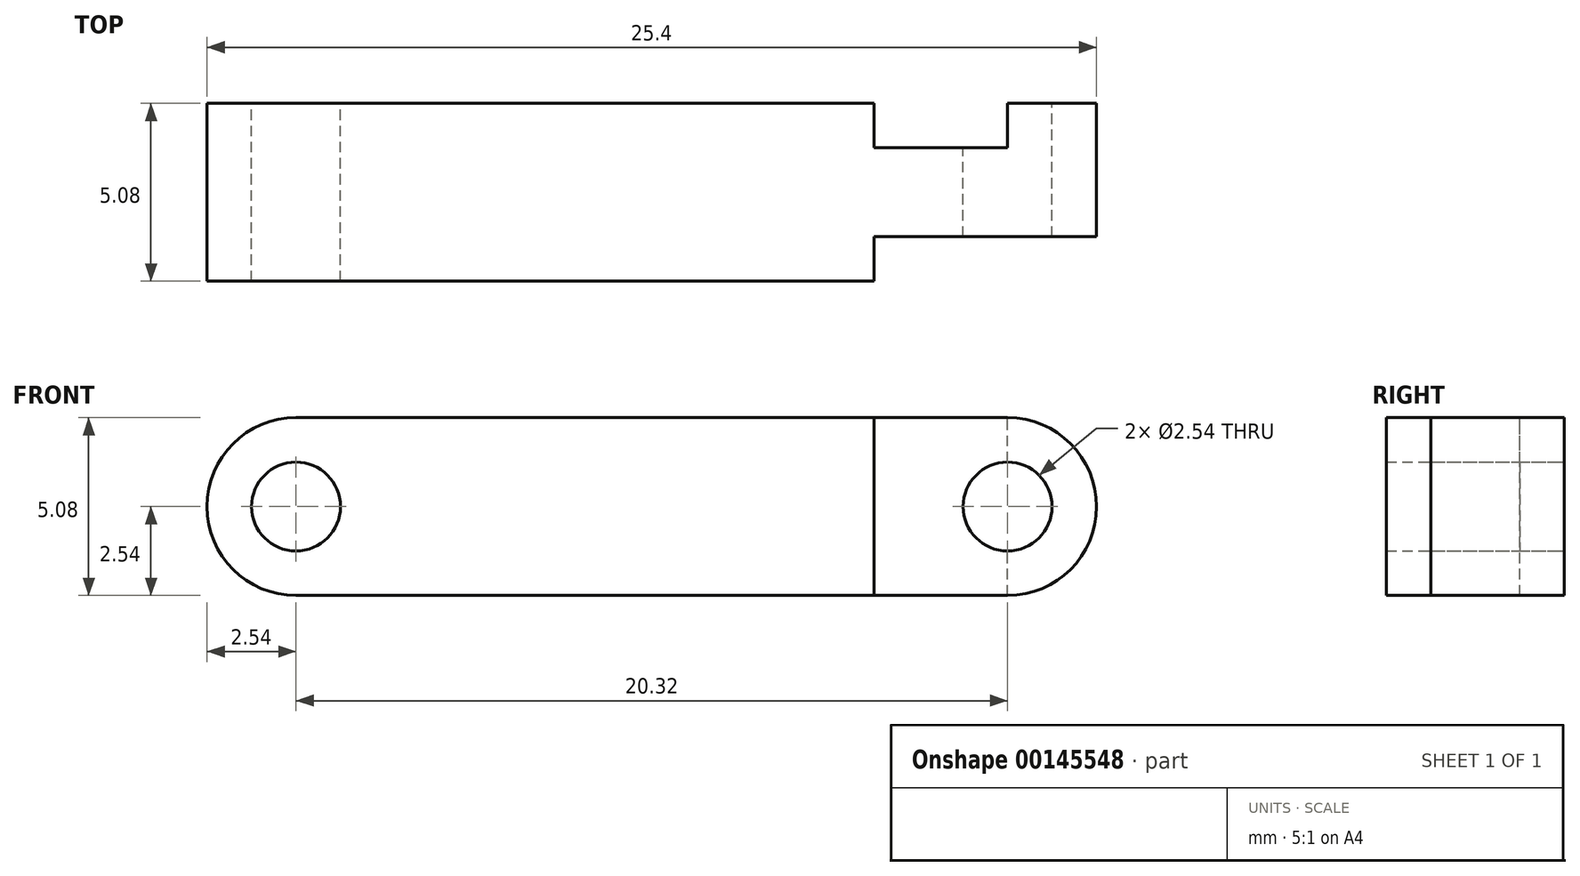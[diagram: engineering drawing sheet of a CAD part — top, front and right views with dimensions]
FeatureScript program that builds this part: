
annotation { "Feature Type Name" : "Feature", "Feature Type Description" : "" }
export const myFeature = defineFeature(function(context is Context, id is Id, definition is map)
    precondition{}
    {
        {
            var Q0;
            Q0=qCreatedBy(makeId("Front.planeOp"),FACE);
            var sketch = newSketch(context, id + "F0", { "sketchPlane" : qUnion([Q0])});
            skLineSegment(sketch, "E0.bottom", {"start": v(0, 0) * mm, "end": v(25.4, 0) * mm});
            skLineSegment(sketch, "E0.top", {"start": v(0, -5.08) * mm, "end": v(25.4, -5.08) * mm});
            skLineSegment(sketch, "E0.left", {"start": v(0, 0) * mm, "end": v(0, -5.08) * mm});
            skLineSegment(sketch, "E0.right", {"start": v(25.4, 0) * mm, "end": v(25.4, -5.08) * mm});
            skCircle(sketch, "E1", {"center": v(22.86, -2.54) * mm, "radius": 1.27 * mm});
            skCircle(sketch, "E2", {"center": v(2.54, -2.54) * mm, "radius": 1.27 * mm});
            skSolve(sketch);
        }
        {
            var Q0;
            Q0 = qSketchRegion(id + "F0", true);
            extrude(context, id + "F1", {"entities" : qUnion([Q0]), "depth" : 5.08 * mm});
        }
        {
            var Q0;
            Q0=makeQuery(id+"F1.opExtrude","SWEPT_EDGE",EDGE,{"disambiguationData":[OSD([sQuery(id+"F0.wireOp",EDGE,"E0.bottom"),sQuery(id+"F0.wireOp",EDGE,"E0.right")])]});
            var Q1;
            Q1=makeQuery(id+"F1.opExtrude","SWEPT_EDGE",EDGE,{"disambiguationData":[OSD([sQuery(id+"F0.wireOp",EDGE,"E0.top"),sQuery(id+"F0.wireOp",EDGE,"E0.right")])]});
            var Q2;
            Q2=makeQuery(id+"F1.opExtrude","SWEPT_EDGE",EDGE,{"disambiguationData":[OSD([sQuery(id+"F0.wireOp",EDGE,"E0.bottom"),sQuery(id+"F0.wireOp",EDGE,"E0.left")])]});
            var Q3;
            Q3=makeQuery(id+"F1.opExtrude","SWEPT_EDGE",EDGE,{"disambiguationData":[OSD([sQuery(id+"F0.wireOp",EDGE,"E0.top"),sQuery(id+"F0.wireOp",EDGE,"E0.left")])]});
            fillet(context, id + "F2", {"entities" : qUnion([Q0, Q1, Q2, Q3]), "radius" : 2.54 * mm, "tangentPropagation" : true, "allowEdgeOverflow" : false});
        }
        {
            var Q0;
            Q0=makeQuery(id+"F1.opExtrude","SWEPT_FACE",FACE,{"disambiguationData":[OSD([sQuery(id+"F0.wireOp",EDGE,"E0.bottom")])]});
            var sketch = newSketch(context, id + "F3", { "sketchPlane" : qUnion([Q0])});
            skLineSegment(sketch, "E3.bottom", {"start": v(19.05, 0) * mm, "end": v(25.4, 0) * mm});
            skLineSegment(sketch, "E3.top", {"start": v(19.05, -5.08) * mm, "end": v(25.4, -5.08) * mm});
            skLineSegment(sketch, "E3.left", {"start": v(19.05, 0) * mm, "end": v(19.05, -5.08) * mm});
            skLineSegment(sketch, "E3.right", {"start": v(25.4, 0) * mm, "end": v(25.4, -5.08) * mm});
            skLineSegment(sketch, "E4.0", {"start": v(2.54, -5.08) * mm, "end": v(22.86, -5.08) * mm});
            skLineSegment(sketch, "E5.0", {"start": v(2.54, 0) * mm, "end": v(22.86, 0) * mm});
            skLineSegment(sketch, "E6.0", {"start": v(22.86, 0) * mm, "end": v(25.4, 0) * mm});
            skLineSegment(sketch, "E7", {"start": v(19.05, -1.27) * mm, "end": v(25.4, -1.27) * mm});
            skLineSegment(sketch, "E8", {"start": v(25.4, -3.81) * mm, "end": v(19.05, -3.81) * mm});
            skSolve(sketch);
        }
        {
            var Q0;
            {var subQ0=sQuery(id+"F3.wireOp",EDGE,"E6.0");Q0=makeQuery(id+"F3.imprint","IMPRINT",FACE,{"disambiguationData":[TD([[makeQuery(id+"F3.imprint","IMPRINT",EDGE,{"derivedFrom":subQ0}),-1.0]])]});}
            var Q1;
            {var subQ0=sQuery(id+"F3.wireOp",EDGE,"E5.0");var subQ1=sQuery(id+"F3.wireOp",EDGE,"E3.left");var subQ2=makeQuery(id+"F3.imprint","INTERSECT",VERTEX,{"derivedFrom":[subQ1,subQ0]});Q1=makeQuery(id+"F3.imprint","IMPRINT",FACE,{"disambiguationData":[TD([[makeQuery(id+"F3.imprint","IMPRINT",EDGE,{"disambiguationData":[TD([[subQ2,-1.0]])],"derivedFrom":subQ1}),1.0]])]});}
            var Q2;
            {var subQ0=sQuery(id+"F3.wireOp",EDGE,"E4.0");var subQ1=sQuery(id+"F3.wireOp",EDGE,"E3.left");var subQ2=makeQuery(id+"F3.imprint","INTERSECT",VERTEX,{"derivedFrom":[subQ1,subQ0]});Q2=makeQuery(id+"F3.imprint","IMPRINT",FACE,{"disambiguationData":[TD([[makeQuery(id+"F3.imprint","IMPRINT",EDGE,{"disambiguationData":[TD([[subQ2,1.0]])],"derivedFrom":subQ1}),1.0]])]});}
            var Q3;
            {var subQ0=sQuery(id+"F3.wireOp",EDGE,"E3.top");Q3=makeQuery(id+"F3.imprint","IMPRINT",FACE,{"disambiguationData":[TD([[makeQuery(id+"F3.imprint","IMPRINT",EDGE,{"derivedFrom":subQ0}),1.0]])]});}
            extrude(context, id + "F4", {"entities" : qUnion([Q0, Q1, Q2, Q3]), "operationType" : NewBodyOperationType.REMOVE, "endBound" : BoundingType.THROUGH_ALL, "oppositeDirection" : true, "depth" : 25.4 * mm});
        }
    });
